# Revit family: FEVH 1 WIDE
name_source: partatom
category: Mechanical Equipment
units: mm (PartAtom-declared; Revit-internal decimal feet)

## family parameters
Always vertical = Yes
Cut with Voids When Loaded = No
Part Type = Normal
Room Calculation Point = No
Round Connector Dimension = Use Diameter
Shared = No
Work Plane-Based = No

## types (7) — shared parameters
Description = 1-fan Evaporator
Fan001 = Yes
HEIGHT = 45.25 "
Manufacturer = Krack Corporation
Overall Width = 36 "
Revit Family Dates = 08/21/2023HM
Type Comments = KR Series 2-Fan Condenser
URL = www.krack.com
WIDTH = 28 "

## per-type parameters (varying)
| type | Copper Pipes | Fan002 | Fan003 | Fan004 | Fan005 | Fan006 | Fan007 | LENGTH | Model | Top Support | Top support visibility |
| FEH 1X4 | <By Category> | Yes | Yes | Yes | No | No | No | 220 " | FEH 1 X 4 | Top Support top : F4 | Yes |
| FEH 1X5 | <By Category> | Yes | Yes | Yes | Yes | No | No | 274 " | FEH 1 X5 | Top Support top : F5 | Yes |
| FEH 1X3 | Copper | Yes | Yes | No | No | No | No | 166 " | FEH 1X3 | Top Support top : F3 | Yes |
| FEH 1X2 | Copper | Yes | No | No | No | No | No | 112 " | FEH 1 X2 | Top Support top : F2 | Yes |
| FEH 1X6 | Copper | Yes | Yes | Yes | Yes | Yes | No | 328 " | FEH 1X6 | Top Support top : F6 | Yes |
| FEH 1X7 | Copper | Yes | Yes | Yes | Yes | Yes | Yes | 382 " | FEH 1 X7 | Top Support top : F7 | Yes |
| FEH 1X1 | Copper | No | No | No | No | No | No | 58 " | FEH 1X1 | Top Support top : F1 | No |

## geometry (parser evidence)
native form markers: Sweep x7
no freeform markers — native parametric forms only
